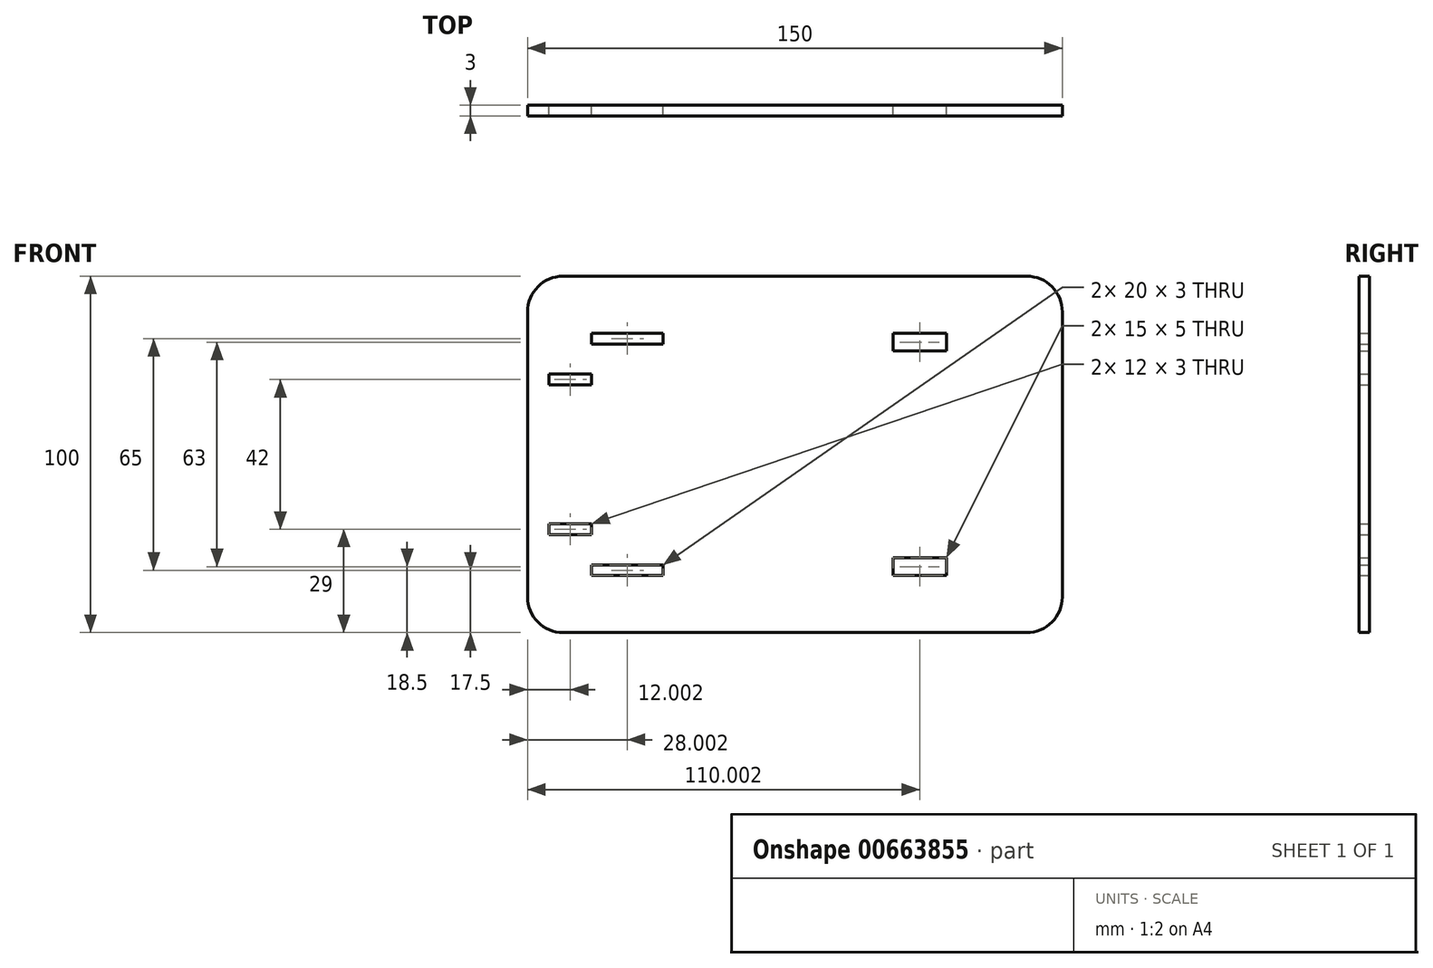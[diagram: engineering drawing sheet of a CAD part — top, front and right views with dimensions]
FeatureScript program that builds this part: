
annotation { "Feature Type Name" : "Feature", "Feature Type Description" : "" }
export const myFeature = defineFeature(function(context is Context, id is Id, definition is map)
    precondition{}
    {
        {
            var Q0;
            Q0=qCreatedBy(makeId("Front.planeOp"),FACE);
            var sketch = newSketch(context, id + "F0", { "sketchPlane" : qUnion([Q0])});
            skLineSegment(sketch, "E0.bottom", {"start": v(66.36, 46.4) * mm, "end": v(-63.64, 46.4) * mm});
            skLineSegment(sketch, "E0.top", {"start": v(66.36, -53.6) * mm, "end": v(-63.64, -53.6) * mm});
            skLineSegment(sketch, "E0.left", {"start": v(76.36, 36.4) * mm, "end": v(76.36, -43.6) * mm});
            skLineSegment(sketch, "E0.right", {"start": v(-73.64, 36.4) * mm, "end": v(-73.64, -43.6) * mm});
            skPoint(sketch, "E1.visualSharp", {"position": v(-73.64, 46.4) * mm});
            skArc(sketch, "E1.filletArc", {"start": v(-63.64, 46.4) * mm, "mid": v(-70.7, 43.48) * mm, "end": v(-73.64, 36.4) * mm});
            skPoint(sketch, "E2.visualSharp", {"position": v(76.36, 46.4) * mm});
            skArc(sketch, "E2.filletArc", {"start": v(76.36, 36.4) * mm, "mid": v(73.43, 43.48) * mm, "end": v(66.36, 46.4) * mm});
            skPoint(sketch, "E3.visualSharp", {"position": v(76.36, -53.6) * mm});
            skArc(sketch, "E3.filletArc", {"start": v(66.36, -53.6) * mm, "mid": v(73.43, -50.66) * mm, "end": v(76.36, -43.6) * mm});
            skPoint(sketch, "E4.visualSharp", {"position": v(-73.64, -53.6) * mm});
            skArc(sketch, "E4.filletArc", {"start": v(-73.64, -43.6) * mm, "mid": v(-70.7, -50.66) * mm, "end": v(-63.64, -53.6) * mm});
            skLineSegment(sketch, "E5.bottom", {"start": v(-55.64, 27.4) * mm, "end": v(-35.64, 27.4) * mm});
            skLineSegment(sketch, "E5.top", {"start": v(-55.64, 30.4) * mm, "end": v(-35.64, 30.4) * mm});
            skLineSegment(sketch, "E5.left", {"start": v(-55.64, 27.4) * mm, "end": v(-55.64, 30.4) * mm});
            skLineSegment(sketch, "E5.right", {"start": v(-35.64, 27.4) * mm, "end": v(-35.64, 30.4) * mm});
            skLineSegment(sketch, "E6.bottom", {"start": v(-67.64, 18.9) * mm, "end": v(-55.64, 18.9) * mm});
            skLineSegment(sketch, "E6.top", {"start": v(-67.64, 15.9) * mm, "end": v(-55.64, 15.9) * mm});
            skLineSegment(sketch, "E6.left", {"start": v(-67.64, 18.9) * mm, "end": v(-67.64, 15.9) * mm});
            skLineSegment(sketch, "E6.right", {"start": v(-55.64, 18.9) * mm, "end": v(-55.64, 15.9) * mm});
            skLineSegment(sketch, "E7.bottom", {"start": v(28.86, 25.4) * mm, "end": v(43.86, 25.4) * mm});
            skLineSegment(sketch, "E7.top", {"start": v(28.86, 30.4) * mm, "end": v(43.86, 30.4) * mm});
            skLineSegment(sketch, "E7.left", {"start": v(28.86, 25.4) * mm, "end": v(28.86, 30.4) * mm});
            skLineSegment(sketch, "E7.right", {"start": v(43.86, 25.4) * mm, "end": v(43.86, 30.4) * mm});
            skLineSegment(sketch, "E8.MirrorCS", {"start": v(-55.64, -26.1) * mm, "end": v(-55.64, -23.1) * mm});
            skLineSegment(sketch, "E9.MirrorCS", {"start": v(43.86, -32.6) * mm, "end": v(43.86, -37.6) * mm});
            skLineSegment(sketch, "E10.MirrorCS", {"start": v(-35.64, -34.6) * mm, "end": v(-35.64, -37.6) * mm});
            skLineSegment(sketch, "E11.MirrorCS", {"start": v(-55.64, -34.6) * mm, "end": v(-55.64, -37.6) * mm});
            skLineSegment(sketch, "E12.MirrorCS", {"start": v(-67.64, -26.1) * mm, "end": v(-67.64, -23.1) * mm});
            skLineSegment(sketch, "E13.MirrorCS", {"start": v(28.86, -32.6) * mm, "end": v(28.86, -37.6) * mm});
            skLineSegment(sketch, "E14.MirrorCS", {"start": v(-67.64, -26.1) * mm, "end": v(-55.64, -26.1) * mm});
            skLineSegment(sketch, "E15.MirrorCS", {"start": v(28.86, -37.6) * mm, "end": v(43.86, -37.6) * mm});
            skLineSegment(sketch, "E16.MirrorCS", {"start": v(-55.64, -37.6) * mm, "end": v(-35.64, -37.6) * mm});
            skLineSegment(sketch, "E17.MirrorCS", {"start": v(-55.64, -34.6) * mm, "end": v(-35.64, -34.6) * mm});
            skLineSegment(sketch, "E18.MirrorCS", {"start": v(-67.64, -23.1) * mm, "end": v(-55.64, -23.1) * mm});
            skLineSegment(sketch, "E19.MirrorCS", {"start": v(28.86, -32.6) * mm, "end": v(43.86, -32.6) * mm});
            skSolve(sketch);
        }
        {
            var Q0;
            Q0=makeQuery(id+"F0.imprint","IMPRINT",FACE,{"disambiguationData":[TD([[makeQuery(id+"F0.imprint","IMPRINT",EDGE,{"derivedFrom":sQuery(id+"F0.wireOp",EDGE,"E0.bottom")}),1.0]])]});
            extrude(context, id + "F1", {"entities" : qUnion([Q0]), "depth" : 3 * mm, "offsetDistance" : 25 * mm});
        }
    });
